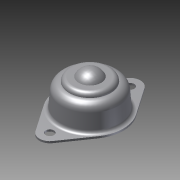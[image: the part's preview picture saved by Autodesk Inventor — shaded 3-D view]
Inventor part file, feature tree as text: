
AUTODESK INVENTOR PART (.ipt)
format: ipt  version: 2011 SP2 (Build 150309200, 309)  size: 145,920 bytes
history: native  units: mm
features: sketch x2, revolve x1, extrude x1
ambient origin geometry x8: Origin, YZ Plane, XZ Plane, XY Plane, X Axis, Y Axis, Z Axis, Center Point
bodies: Solid1 (feature_tree)
feature tree (4):
  revolve  "Revolution1"  [1 undecoded]
  extrude  "Extrusion1"  Depth=34.9mm
  sketch  "Sketch1"  dims[d10=90.0deg d11=4.0mm]
  sketch  "Sketch2"  dims[d12=4.0mm d13=34.9mm d14=19.45mm d15=10.0mm d16=10.0mm d17=32.1mm d18=0.9mm d19=0.0mm]
note: 1 required parameter value undecoded (feature->parameter linkage not recoverable at this tier; creation-order binding heuristic only, values carry confidence <= 0.55)
